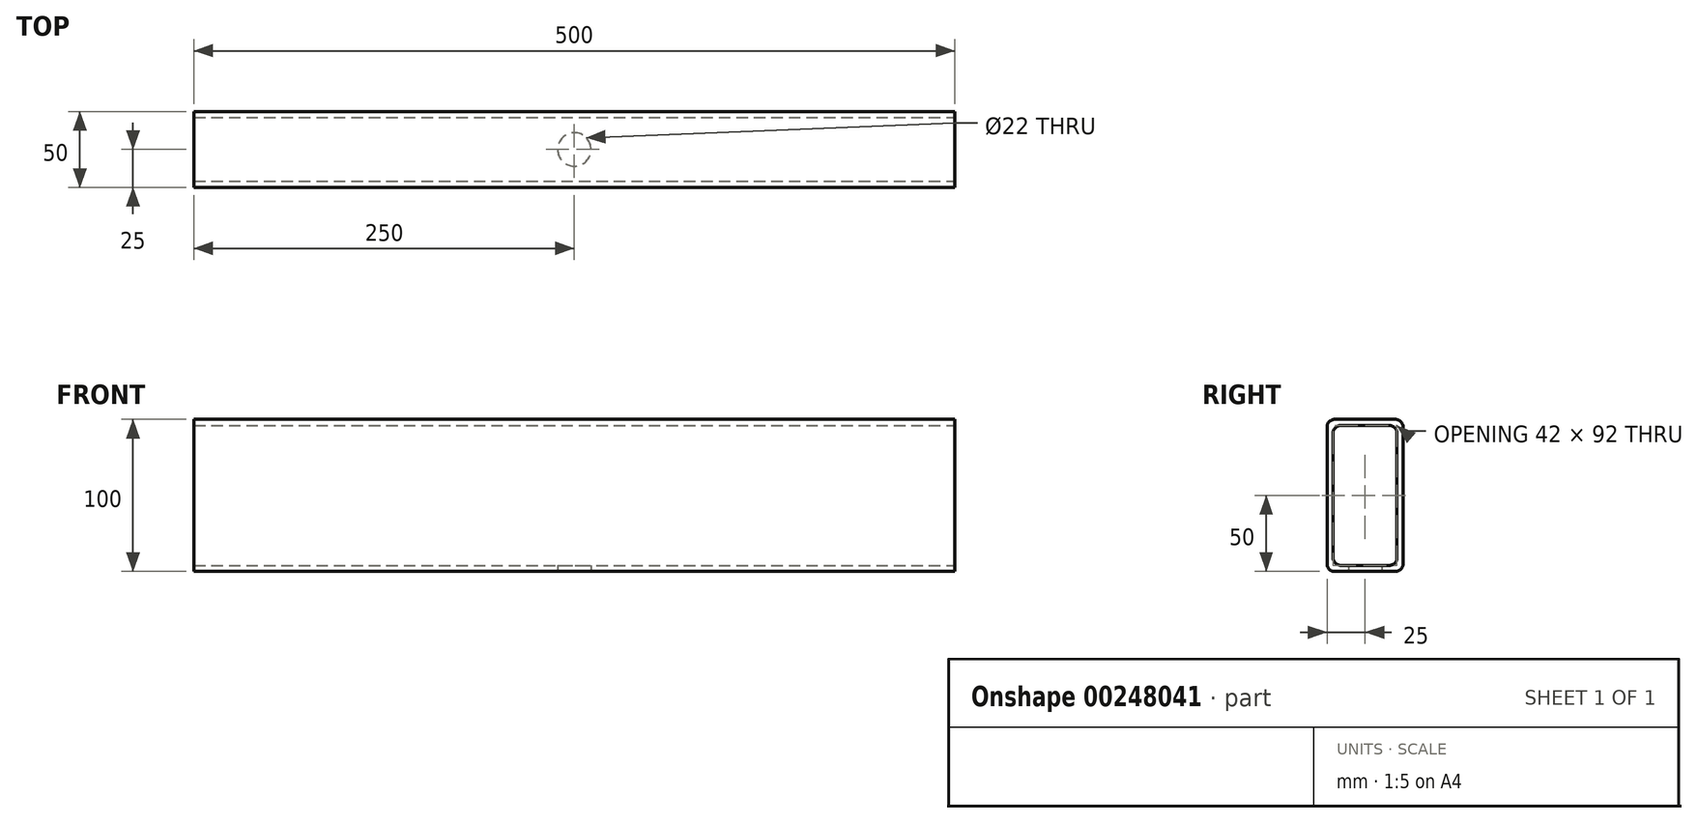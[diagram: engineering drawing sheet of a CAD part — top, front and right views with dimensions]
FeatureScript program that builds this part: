
annotation { "Feature Type Name" : "Feature", "Feature Type Description" : "" }
export const myFeature = defineFeature(function(context is Context, id is Id, definition is map)
    precondition{}
    {
        {
            var Q0;
            Q0=qCreatedBy(makeId("Front.planeOp"),FACE);
            var sketch = newSketch(context, id + "F0", { "sketchPlane" : qUnion([Q0])});
            skLineSegment(sketch, "E0.bottom", {"start": v(-250, 50) * mm, "end": v(250, 50) * mm});
            skLineSegment(sketch, "E0.top", {"start": v(-150, -50) * mm, "end": v(250, -50) * mm});
            skLineSegment(sketch, "E0.right", {"start": v(250, 50) * mm, "end": v(250, -50) * mm});
            skPoint(sketch, "E0.middle", {"position": v(0, 0) * mm});
            skPoint(sketch, "E1", {"position": v(-150, -50) * mm});
            skPoint(sketch, "E2.orphan", {"position": v(-250, -50) * mm});
            skLineSegment(sketch, "E3", {"start": v(-250, 50) * mm, "end": v(-250, -50) * mm});
            skLineSegment(sketch, "E4", {"start": v(-250, -50) * mm, "end": v(-150, -50) * mm});
            skSolve(sketch);
        }
        {
            var Q0;
            Q0=makeQuery(id+"F0.imprint","IMPRINT",FACE,{"disambiguationData":[TD([[makeQuery(id+"F0.imprint","IMPRINT",EDGE,{"derivedFrom":sQuery(id+"F0.wireOp",EDGE,"E0.bottom")}),-1.0]])]});
            extrude(context, id + "F1", {"entities" : qUnion([Q0]), "depth" : 50 * mm});
        }
        {
            var Q0;
            Q0=makeQuery(id+"F1.opExtrude","SWEPT_FACE",FACE,{"disambiguationData":[OSD([sQuery(id+"F0.wireOp",EDGE,"iOPjKeeN-IbBG-J6lS-LW06-ZQlqX36HwCFS")])]});
            var Q1;
            Q1=makeQuery(id+"F1.opExtrude","SWEPT_FACE",FACE,{"disambiguationData":[OSD([sQuery(id+"F0.wireOp",EDGE,"E0.right")])]});
            var Q2;
            Q2=makeQuery(id+"F1.opExtrude","SWEPT_FACE",FACE,{"disambiguationData":[OSD([sQuery(id+"F0.wireOp",EDGE,"E3")])]});
            shell(context, id + "F2", {"entities" : qUnion([Q0, Q1, Q2]), "thickness" : 4 * mm});
        }
        {
            var Q0;
            Q0=makeQuery(id+"F1.opExtrude","SWEPT_FACE",FACE,{"disambiguationData":[OSD([sQuery(id+"F0.wireOp",EDGE,"E0.top")])]});
            var sketch = newSketch(context, id + "F3", { "sketchPlane" : qUnion([Q0])});
            skPoint(sketch, "E5", {"position": v(0, 25) * mm});
            skSolve(sketch);
        }
        {
            var Q0;
            Q0=sQuery(id+"F3.wireOp",VERTEX,"E5");
            var Q1;
            Q1=makeQuery(id+"F1.opExtrude","SWEPT_BODY",BODY,{"disambiguationData":[OSD([sQuery(id+"F0.wireOp",EDGE,"E0.bottom"),sQuery(id+"F0.wireOp",EDGE,"E0.top"),sQuery(id+"F0.wireOp",EDGE,"E0.right"),sQuery(id+"F0.wireOp",EDGE,"iOPjKeeN-IbBG-J6lS-LW06-ZQlqX36HwCFS")])]});
            hole(context, id + "F4", {"style" : HoleStyle.SIMPLE, "endStyle" : HoleEndStyle.BLIND, "holeDiameter" : 22 * mm, "holeDepth" : 4 * mm, "tappedDepth" : 12 * mm, "tapClearance" : 3, "locations" : qUnion([Q0]), "scope" : qUnion([Q1])});
        }
        {
            var Q0;
            Q0=makeQuery(id+"F1.opExtrude","CAP_EDGE",EDGE,{"disambiguationData":[OSD([sQuery(id+"F0.wireOp",EDGE,"E0.bottom")])],"isStart":false});
            var Q1;
            Q1=makeQuery(id+"F1.opExtrude","CAP_EDGE",EDGE,{"disambiguationData":[OSD([sQuery(id+"F0.wireOp",EDGE,"E0.top")])],"isStart":false});
            var Q2;
            Q2=makeQuery(id+"F1.opExtrude","CAP_EDGE",EDGE,{"disambiguationData":[OSD([sQuery(id+"F0.wireOp",EDGE,"E0.top")])],"isStart":true});
            var Q3;
            Q3=makeQuery(id+"F1.opExtrude","CAP_EDGE",EDGE,{"disambiguationData":[OSD([sQuery(id+"F0.wireOp",EDGE,"E0.bottom")])],"isStart":true});
            var Q4;
            {var subQ0=sQuery(id+"F0.wireOp",EDGE,"E0.top");Q4=makeQuery(id+"F2.opShell","OFFSET_EDGE",EDGE,{"disambiguationData":[OSD([subQ0]),TDD([makeQuery(id+"F1.opExtrude","CAP_EDGE",EDGE,{"disambiguationData":[OSD([subQ0])],"isStart":true})])]});}
            var Q5;
            {var subQ0=sQuery(id+"F0.wireOp",EDGE,"E0.top");Q5=makeQuery(id+"F2.opShell","OFFSET_EDGE",EDGE,{"disambiguationData":[OSD([subQ0]),TDD([makeQuery(id+"F1.opExtrude","CAP_EDGE",EDGE,{"disambiguationData":[OSD([subQ0])],"isStart":false})])]});}
            var Q6;
            {var subQ0=sQuery(id+"F0.wireOp",EDGE,"E0.bottom");Q6=makeQuery(id+"F2.opShell","OFFSET_EDGE",EDGE,{"disambiguationData":[OSD([subQ0]),TDD([makeQuery(id+"F1.opExtrude","CAP_EDGE",EDGE,{"disambiguationData":[OSD([subQ0])],"isStart":false})])]});}
            var Q7;
            {var subQ0=sQuery(id+"F0.wireOp",EDGE,"E0.bottom");Q7=makeQuery(id+"F2.opShell","OFFSET_EDGE",EDGE,{"disambiguationData":[OSD([subQ0]),TDD([makeQuery(id+"F1.opExtrude","CAP_EDGE",EDGE,{"disambiguationData":[OSD([subQ0])],"isStart":true})])]});}
            fillet(context, id + "F5", {"entities" : qUnion([Q0, Q1, Q2, Q3, Q4, Q5, Q6, Q7]), "radius" : 5 * mm, "tangentPropagation" : true, "allowEdgeOverflow" : false});
        }
    });
